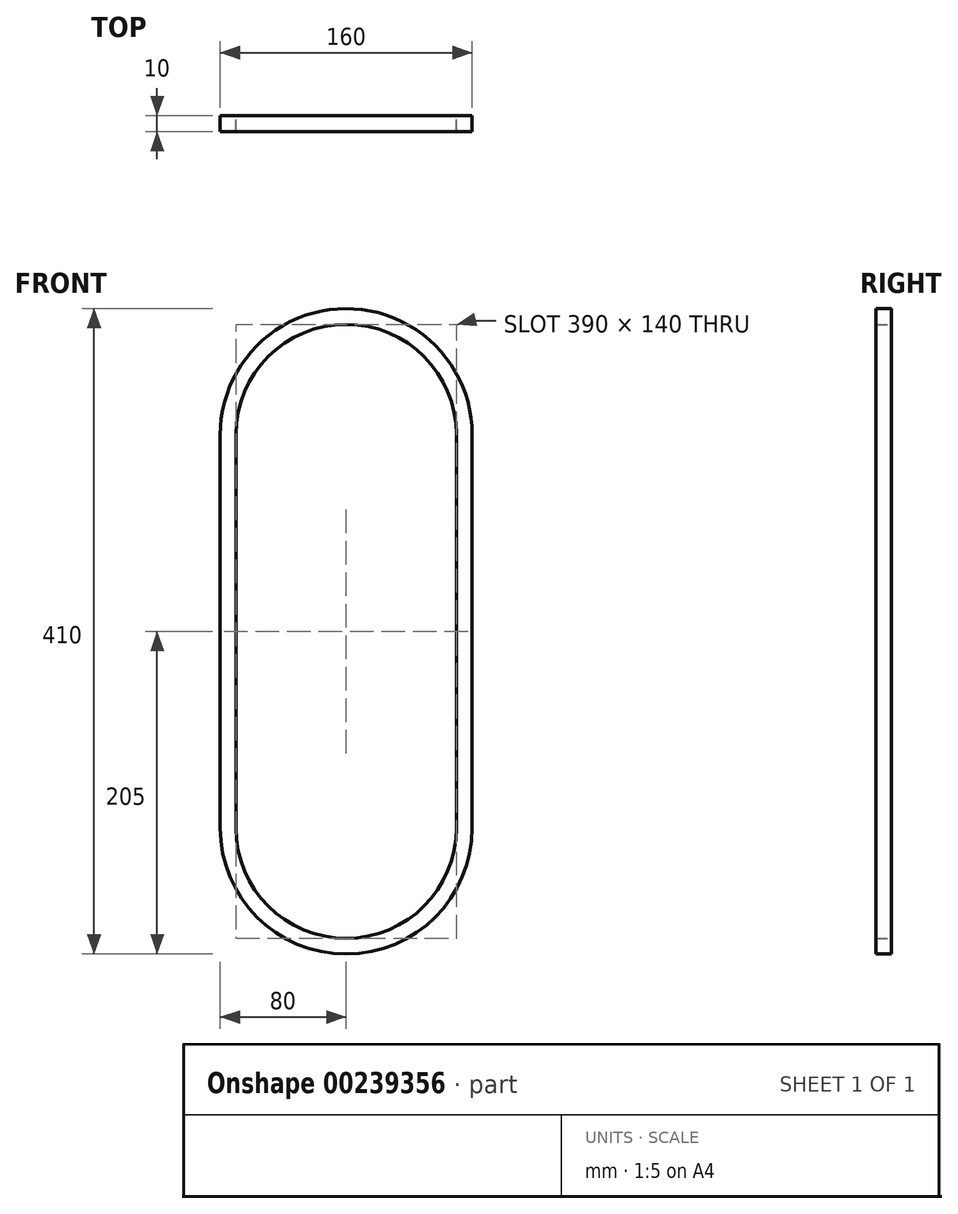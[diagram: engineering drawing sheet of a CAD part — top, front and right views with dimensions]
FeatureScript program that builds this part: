
annotation { "Feature Type Name" : "Feature", "Feature Type Description" : "" }
export const myFeature = defineFeature(function(context is Context, id is Id, definition is map)
    precondition{}
    {
        {
            var Q0;
            Q0=qCreatedBy(makeId("Front.planeOp"),FACE);
            var sketch = newSketch(context, id + "F0", { "sketchPlane" : qUnion([Q0])});
            skArc(sketch, "E0", {"start": v(70, 0) * mm, "mid": v(0, 70) * mm, "end": v(-70, 0) * mm});
            skArc(sketch, "E1", {"start": v(-70, -250) * mm, "mid": v(0, -320) * mm, "end": v(70, -250) * mm});
            skArc(sketch, "E2", {"start": v(80, 0) * mm, "mid": v(-0.18, 80) * mm, "end": v(-80, -0.37) * mm});
            skArc(sketch, "E3", {"start": v(-80, -250) * mm, "mid": v(0, -330) * mm, "end": v(80, -250) * mm});
            skLineSegment(sketch, "E4", {"start": v(-70, 0) * mm, "end": v(-70, -250) * mm});
            skLineSegment(sketch, "E5", {"start": v(70, 0) * mm, "end": v(70, -250) * mm});
            skLineSegment(sketch, "E6", {"start": v(80, 0) * mm, "end": v(80, -250) * mm});
            skPoint(sketch, "E7.orphan", {"position": v(-70, -155.32) * mm});
            skLineSegment(sketch, "E8", {"start": v(-80, -250) * mm, "end": v(-80, -0.37) * mm});
            skSolve(sketch);
        }
        {
            var Q0;
            Q0=makeQuery(id+"F0.imprint","IMPRINT",FACE,{"disambiguationData":[TD([[makeQuery(id+"F0.imprint","IMPRINT",EDGE,{"derivedFrom":sQuery(id+"F0.wireOp",EDGE,"E0")}),-1.0]])]});
            extrude(context, id + "F1", {"entities" : qUnion([Q0]), "depth" : 10 * mm});
        }
    });
